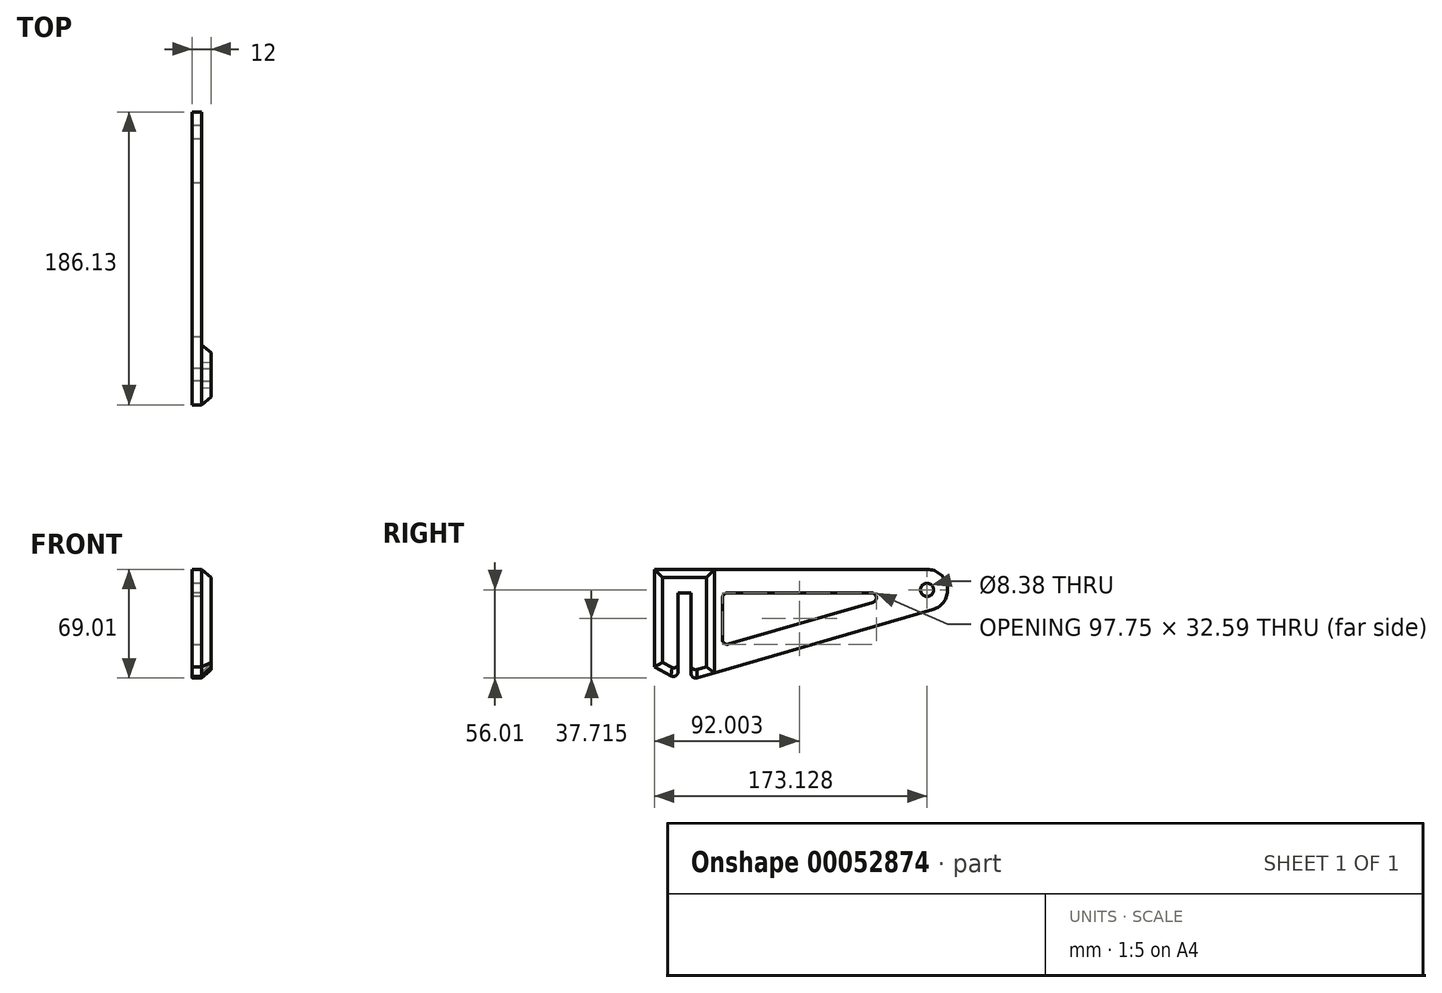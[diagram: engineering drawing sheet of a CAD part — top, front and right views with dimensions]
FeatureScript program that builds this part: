
annotation { "Feature Type Name" : "Feature", "Feature Type Description" : "" }
export const myFeature = defineFeature(function(context is Context, id is Id, definition is map)
    precondition{}
    {
        {
            var Q0;
            Q0=qCreatedBy(makeId("Right.planeOp"),FACE);
            var sketch = newSketch(context, id + "F0", { "sketchPlane" : qUnion([Q0])});
            skLineSegment(sketch, "E0.top", {"start": v(0, 55) * mm, "end": v(8.13, 55) * mm});
            skLineSegment(sketch, "E0.left", {"start": v(0, 0) * mm, "end": v(0, 55) * mm});
            skLineSegment(sketch, "E0.right", {"start": v(8.13, 0) * mm, "end": v(8.13, 55) * mm});
            skLineSegment(sketch, "E1", {"start": v(-15, 70) * mm, "end": v(-15, 8) * mm});
            skLineSegment(sketch, "E2", {"start": v(-15, 8) * mm, "end": v(0, 0) * mm});
            skLineSegment(sketch, "E3", {"start": v(-15, 70) * mm, "end": v(158.13, 70) * mm});
            skArc(sketch, "E4", {"start": v(161.75, 44.51) * mm, "mid": v(171, 58.83) * mm, "end": v(158.13, 70) * mm});
            skLineSegment(sketch, "E5", {"start": v(8.13, 0) * mm, "end": v(161.75, 44.51) * mm});
            skLineSegment(sketch, "E6", {"start": v(28.13, 55) * mm, "end": v(28.13, 21.41) * mm});
            skLineSegment(sketch, "E7", {"start": v(28.13, 55) * mm, "end": v(144.04, 55) * mm});
            skLineSegment(sketch, "E8", {"start": v(28.13, 21.41) * mm, "end": v(144.04, 55) * mm});
            skCircle(sketch, "E9", {"center": v(158.13, 57) * mm, "radius": 4.2 * mm});
            skSolve(sketch);
        }
        {
            var Q0;
            Q0=makeQuery(id+"F0.imprint","IMPRINT",FACE,{"disambiguationData":[TD([[makeQuery(id+"F0.imprint","IMPRINT",EDGE,{"derivedFrom":sQuery(id+"F0.wireOp",EDGE,"E0.top")}),1.0]])]});
            extrude(context, id + "F1", {"entities" : qUnion([Q0]), "depth" : 6 * mm});
        }
        {
            var Q0;
            Q0=makeQuery(id+"F1.opExtrude","SWEPT_EDGE",EDGE,{"disambiguationData":[OSD([sQuery(id+"F0.wireOp",EDGE,"E7"),sQuery(id+"F0.wireOp",EDGE,"E8")])]});
            var Q1;
            Q1=makeQuery(id+"F1.opExtrude","SWEPT_EDGE",EDGE,{"disambiguationData":[OSD([sQuery(id+"F0.wireOp",EDGE,"E6"),sQuery(id+"F0.wireOp",EDGE,"E7")])]});
            var Q2;
            Q2=makeQuery(id+"F1.opExtrude","SWEPT_EDGE",EDGE,{"disambiguationData":[OSD([sQuery(id+"F0.wireOp",EDGE,"E6"),sQuery(id+"F0.wireOp",EDGE,"E8")])]});
            var Q3;
            Q3=makeQuery(id+"F1.opExtrude","SWEPT_EDGE",EDGE,{"disambiguationData":[OSD([sQuery(id+"F0.wireOp",EDGE,"E0.right"),sQuery(id+"F0.wireOp",EDGE,"E5")])]});
            var Q4;
            Q4=makeQuery(id+"F1.opExtrude","SWEPT_EDGE",EDGE,{"disambiguationData":[OSD([sQuery(id+"F0.wireOp",EDGE,"E0.left"),sQuery(id+"F0.wireOp",EDGE,"E2")])]});
            fillet(context, id + "F2", {"entities" : qUnion([Q0, Q1, Q2, Q3, Q4]), "radius" : 3 * mm, "tangentPropagation" : true, "allowEdgeOverflow" : false});
        }
        {
            var Q0;
            Q0=makeQuery(id+"F1.opExtrude","CAP_FACE",FACE,{"disambiguationData":[OSD([sQuery(id+"F0.wireOp",EDGE,"E0.top"),sQuery(id+"F0.wireOp",EDGE,"E0.left"),sQuery(id+"F0.wireOp",EDGE,"E0.right"),sQuery(id+"F0.wireOp",EDGE,"E1"),sQuery(id+"F0.wireOp",EDGE,"E2"),sQuery(id+"F0.wireOp",EDGE,"E3"),sQuery(id+"F0.wireOp",EDGE,"E4"),sQuery(id+"F0.wireOp",EDGE,"E5"),sQuery(id+"F0.wireOp",EDGE,"E6"),sQuery(id+"F0.wireOp",EDGE,"E7"),sQuery(id+"F0.wireOp",EDGE,"E8"),sQuery(id+"F0.wireOp",EDGE,"E9")])],"isStart":false});
            var sketch = newSketch(context, id + "F3", { "sketchPlane" : qUnion([Q0])});
            skLineSegment(sketch, "E10", {"start": v(-15, 70) * mm, "end": v(23.13, 70) * mm});
            skLineSegment(sketch, "E11", {"start": v(8.13, 55) * mm, "end": v(0, 55) * mm});
            skPoint(sketch, "E12.orphan", {"position": v(28.13, 70) * mm});
            skPoint(sketch, "E13.orphan", {"position": v(28.13, 33.66) * mm});
            skLineSegment(sketch, "E14", {"start": v(23.13, 70) * mm, "end": v(23.13, 4.35) * mm});
            skLineSegment(sketch, "E15", {"start": v(-15, 70) * mm, "end": v(-15, 8) * mm});
            skLineSegment(sketch, "E16.0", {"start": v(0, 5) * mm, "end": v(0, 55) * mm});
            skLineSegment(sketch, "E17.0", {"start": v(8.13, 4) * mm, "end": v(8.13, 55) * mm});
            skArc(sketch, "E18.0", {"start": v(8.13, 4) * mm, "mid": v(9.33, 1.6) * mm, "end": v(11.96, 1.11) * mm});
            skLineSegment(sketch, "E19", {"start": v(23.13, 4.35) * mm, "end": v(11.96, 1.11) * mm});
            skArc(sketch, "E20.0", {"start": v(-4.41, 2.35) * mm, "mid": v(-1.46, 2.43) * mm, "end": v(0, 5) * mm});
            skLineSegment(sketch, "E21", {"start": v(-15, 8) * mm, "end": v(-4.41, 2.35) * mm});
            skSolve(sketch);
        }
        {
            var Q0;
            {var subQ6=sQuery(id+"F3.wireOp",EDGE,"E10");Q0=makeQuery(id+"F3.imprint","IMPRINT",FACE,{"disambiguationData":[TD([[makeQuery(id+"F3.imprint","IMPRINT",EDGE,{"derivedFrom":subQ6}),-1.0]])]});}
            cPlane(context, id + "F4", {"entities" : qUnion([Q0]), "cplaneType" : CPlaneType.OFFSET, "offset" : 6 * mm, "width" : 150 * mm, "height" : 150 * mm});
        }
        {
            var Q0;
            Q0=qCreatedBy(id+"F4.planeOp",FACE);
            var sketch = newSketch(context, id + "F5", { "sketchPlane" : qUnion([Q0])});
            skLineSegment(sketch, "E22.2", {"start": v(18.13, 8.1) * mm, "end": v(18.13, 65) * mm});
            skLineSegment(sketch, "E22.4", {"start": v(18.13, 65) * mm, "end": v(-10, 65) * mm});
            skLineSegment(sketch, "E22.5", {"start": v(-10, 65) * mm, "end": v(-10, 11) * mm});
            skLineSegment(sketch, "E23", {"start": v(18.13, 8.1) * mm, "end": v(12.13, 6.36) * mm});
            skLineSegment(sketch, "E24", {"start": v(-10, 11) * mm, "end": v(-4, 7.8) * mm});
            skLineSegment(sketch, "E25.0", {"start": v(0, 55) * mm, "end": v(8.13, 55) * mm});
            skLineSegment(sketch, "E26.0", {"start": v(0, 10.2) * mm, "end": v(0, 55) * mm});
            skLineSegment(sketch, "E27.0", {"start": v(8.13, 4) * mm, "end": v(8.13, 55) * mm});
            skArc(sketch, "E28", {"start": v(-4, 7.8) * mm, "mid": v(-1.32, 7.87) * mm, "end": v(0, 10.2) * mm});
            skArc(sketch, "E29", {"start": v(8.13, 9.37) * mm, "mid": v(9.38, 6.87) * mm, "end": v(12.13, 6.36) * mm});
            skSolve(sketch);
        }
        {
            var Q1;
            Q1=makeQuery(id+"F3.imprint","IMPRINT",FACE,{"disambiguationData":[TD([[makeQuery(id+"F3.imprint","IMPRINT",EDGE,{"derivedFrom":sQuery(id+"F3.wireOp",EDGE,"E10")}),-1.0]])]});
            var Q2;
            Q2=makeQuery(id+"F5.imprint","IMPRINT",FACE,{"disambiguationData":[TD([[makeQuery(id+"F5.imprint","IMPRINT",EDGE,{"derivedFrom":sQuery(id+"F5.wireOp",EDGE,"E22.2")}),1.0]])]});
            loft(context, id + "F6", {"operationType" : NewBodyOperationType.ADD, "sheetProfilesArray" : [{ "sheetProfileEntities" : qUnion([Q1]) }, { "sheetProfileEntities" : qUnion([Q2]) }]});
        }
    });
